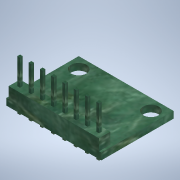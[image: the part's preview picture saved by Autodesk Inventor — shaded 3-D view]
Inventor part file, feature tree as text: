
AUTODESK INVENTOR PART (.ipt)
format: ipt  version: 2020.2 (Build 242310000, 310)  size: 220,160 bytes
history: native  units: mm
features: sketch x4, extrude x3, hole x1
ambient origin geometry x8: Origin, YZ Plane, XZ Plane, XY Plane, X Axis, Y Axis, Z Axis, Center Point
bodies: Solido1 (feature_tree)
feature tree (8):
  extrude  "Estrusione1"  Depth=16.0mm
  hole  "Foro1"  [1 undecoded]
  extrude  "Estrusione2"  Depth=1.5mm TaperAngle=0.0deg
  extrude  "Estrusione3"  Depth=2.5mm
  sketch  "Schizzo1"
  sketch  "Schizzo2"
  sketch  "Schizzo4"
  sketch  "Schizzo6"
note: 1 required parameter value undecoded (feature->parameter linkage not recoverable at this tier; creation-order binding heuristic only, values carry confidence <= 0.55)
